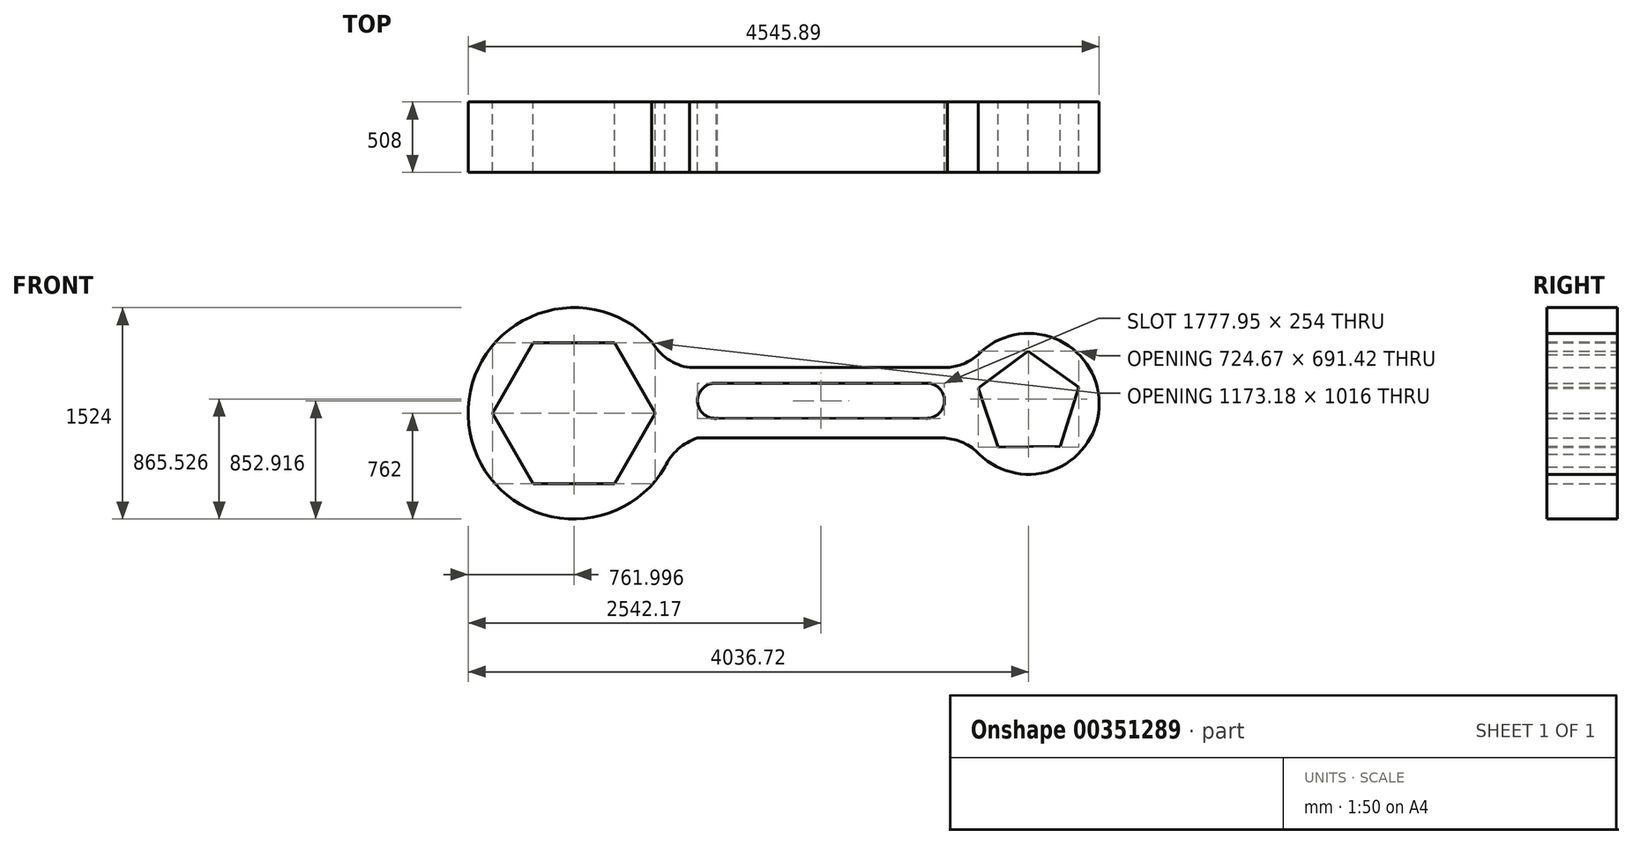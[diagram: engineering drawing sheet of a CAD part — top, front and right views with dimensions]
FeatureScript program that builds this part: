
annotation { "Feature Type Name" : "Feature", "Feature Type Description" : "" }
export const myFeature = defineFeature(function(context is Context, id is Id, definition is map)
    precondition{}
    {
        {
            var Q0;
            Q0=qCreatedBy(makeId("Front.planeOp"),FACE);
            var sketch = newSketch(context, id + "F0", { "sketchPlane" : qUnion([Q0])});
            skCircle(sketch, "E0", {"center": v(-1781.46, -235.64) * mm, "radius": 762 * mm});
            skCircle(sketch, "E1", {"center": v(1494.43, -167.39) * mm, "radius": 508 * mm});
            skArc(sketch, "E2", {"start": v(-755.33, -17.97) * mm, "mid": v(-890.26, -148.23) * mm, "end": v(-748.35, -270.84) * mm});
            skArc(sketch, "E3", {"start": v(760.61, -271.72) * mm, "mid": v(887.69, -144.75) * mm, "end": v(760.67, -17.72) * mm});
            skLineSegment(sketch, "E4", {"start": v(-755.33, -17.97) * mm, "end": v(760.67, -17.72) * mm});
            skLineSegment(sketch, "E5", {"start": v(-778.42, -270.82) * mm, "end": v(760.61, -271.72) * mm});
            skLineSegment(sketch, "E6.0", {"start": v(1130.93, -53.24) * mm, "end": v(1490.66, 213.6) * mm});
            skLineSegment(sketch, "E6.1", {"start": v(1490.66, 213.6) * mm, "end": v(1855.6, -46.07) * mm});
            skLineSegment(sketch, "E6.2", {"start": v(1855.6, -46.07) * mm, "end": v(1721.4, -473.4) * mm});
            skLineSegment(sketch, "E6.3", {"start": v(1721.4, -473.4) * mm, "end": v(1273.54, -477.82) * mm});
            skLineSegment(sketch, "E6.4", {"start": v(1273.54, -477.82) * mm, "end": v(1130.93, -53.24) * mm});
            skPoint(sketch, "E6.0.midPoint", {"position": v(1310.8, 80.18) * mm});
            skLineSegment(sketch, "E7.0", {"start": v(-2074.76, 272.36) * mm, "end": v(-1488.17, 272.36) * mm});
            skLineSegment(sketch, "E7.1", {"start": v(-1488.17, 272.36) * mm, "end": v(-1194.88, -235.64) * mm});
            skLineSegment(sketch, "E7.2", {"start": v(-1194.88, -235.64) * mm, "end": v(-1488.17, -743.64) * mm});
            skLineSegment(sketch, "E7.3", {"start": v(-1488.17, -743.64) * mm, "end": v(-2074.76, -743.64) * mm});
            skLineSegment(sketch, "E7.4", {"start": v(-2074.76, -743.64) * mm, "end": v(-2368.05, -235.64) * mm});
            skLineSegment(sketch, "E7.5", {"start": v(-2368.05, -235.64) * mm, "end": v(-2074.76, 272.36) * mm});
            skPoint(sketch, "E7.0.midPoint", {"position": v(-1781.46, 272.36) * mm});
            skLineSegment(sketch, "E8", {"start": v(-947.26, 93.9) * mm, "end": v(908.24, 93.9) * mm});
            skLineSegment(sketch, "E9", {"start": v(-890.26, -414.1) * mm, "end": v(889.43, -414.1) * mm});
            skArc(sketch, "E10", {"start": v(-1220.98, 280.6) * mm, "mid": v(-1105.48, 155.94) * mm, "end": v(-947.26, 93.9) * mm});
            skArc(sketch, "E11", {"start": v(-890.26, -414.1) * mm, "mid": v(-1030.33, -493.18) * mm, "end": v(-1125.28, -623.02) * mm});
            skPoint(sketch, "E11.startSnap0", {"position": v(-890.26, -148.23) * mm});
            skArc(sketch, "E12", {"start": v(908.24, 93.9) * mm, "mid": v(1026.54, 122.23) * mm, "end": v(1129.88, 186.4) * mm});
            skArc(sketch, "E13", {"start": v(1139.12, -530.46) * mm, "mid": v(1025.16, -448.92) * mm, "end": v(889.43, -414.1) * mm});
            skSolve(sketch);
        }
        {
            var Q0;
            {var subQ11=sQuery(id+"F0.wireOp",EDGE,"E3");Q0=makeQuery(id+"F0.imprint","IMPRINT",FACE,{"disambiguationData":[TD([[makeQuery(id+"F0.imprint","IMPRINT",EDGE,{"derivedFrom":subQ11}),-1.0]])]});}
            var Q1;
            Q1=makeQuery(id+"F0.imprint","IMPRINT",FACE,{"disambiguationData":[TD([[makeQuery(id+"F0.imprint","IMPRINT",EDGE,{"derivedFrom":sQuery(id+"F0.wireOp",EDGE,"E7.0")}),1.0]])]});
            var Q2;
            Q2=makeQuery(id+"F0.imprint","IMPRINT",FACE,{"disambiguationData":[TD([[makeQuery(id+"F0.imprint","IMPRINT",EDGE,{"derivedFrom":sQuery(id+"F0.wireOp",EDGE,"E6.0")}),1.0]])]});
            extrude(context, id + "F1", {"entities" : qUnion([Q0, Q1, Q2]), "depth" : 508 * mm});
        }
    });
